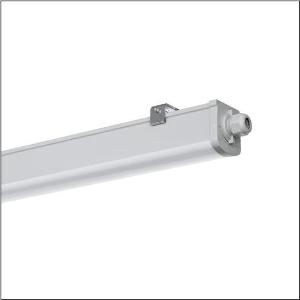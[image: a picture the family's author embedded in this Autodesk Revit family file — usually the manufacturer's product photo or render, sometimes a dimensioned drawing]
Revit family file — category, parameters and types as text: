
# Revit family: monsun_r__31_51fa20dk450b_5819
name_source: partatom
category: Lighting Fixtures
units: mm (PartAtom-declared; Revit-internal decimal feet)

## family parameters
Cut with Voids When Loaded = No
Host = Face
Light Source = No
Part Type = Normal
Room Calculation Point = No
Round Connector Dimension = Use Diameter
Shared = No

## types (1)
- Monsun® 31 (1 x LED, 5100 lm, 38 W, 4000K)
    Apparent Load = 38 VA
    CIE Flux Codes = 42 72 91 92 100
    Color Rendering = 80
    Color Temperature = 4000K
    Default Elevation = 1800 mm
    Description = Monsun® 31, damp-proof luminaire, primary optical cover: diffuser, of PC, frosted, light emission: direct distribution, primary light characteristic: symmetric, installation type: surface-mounted, LED, rated luminous flux: 5.100lm, luminous efficacy: 134lm/W, light colour: 840, colour temperature: 4000K, control gear: ECG, with terminal, 5+1-pole, max. 2.5mm², through-wiring: 3x 2.5mm² + 3x 1.5mm², mains connection: 220..240V, AC, 50/60Hz, rated input power: 38W, housing, luminaire housing, of PC, light grey (RAL 7035), length: 1.158mm, width: 68mm, height: 76mm, protection rating (complete): IP66, insulation class (complete): insulation class II (safety insulation), certification: CE, ENEC, UKCA, protection symbol: D, impact resistance: IK08, permissible operating ambient temperature: -20..+40°C, corresponds to IFS (International Featured Standards) requirements for safety and quality in the food industry, contact your sales advisor before using the luminaires in applications with unclear chemical exposure, large temperature fluctuations or condensation-forming humidity, packaging unit: 1 piece
    Height = 77 mm
    Lamp = 1 x LED
    Lamp Light Flux = 5100 lm
    Lamp Power = 38 W
    Lamp count = 1
    Length = 1218 mm
    Luminous efficacy = 134 lm/W
    Manufacturer = Siteco
    ModVariant = No
    Model = 51FA20DK450B
    Mounting Place = Ceiling
    Mounting Type = Surface mounted
    Number of Poles = 1
    OnlyDefault = Yes
    Power Factor = 1
    Product Name = Monsun® 31
    Product group = damp-proof luminaire
    ProductGroupID = 300
    Protection Class = Protection class II
    Protection Degree = IP 66
    RLX_Detail_Level = 1
    RLX_Emergency_Light_Flux = 0 lm
    RLX_Emergency_Type = 0
    RLX_Emergency_Type_DB = No
    RlxData = <blob elided: 32953 chars, md5=dea1a023>
    Socket = socket
    Standby Power = 0 W
    System Light Flux = 5100 lm
    System Power = 38 W
    Type Comments = Product without accessories
    Type Image = l_1006174.jpg
    URL = http://relux.com
    VarID = ---
    Voltage = 0 V
    Weight = 0.00 kg
    Width = 69 mm

## geometry (parser evidence)
native form markers: Blend x4, Sweep x12
no freeform markers — native parametric forms only
